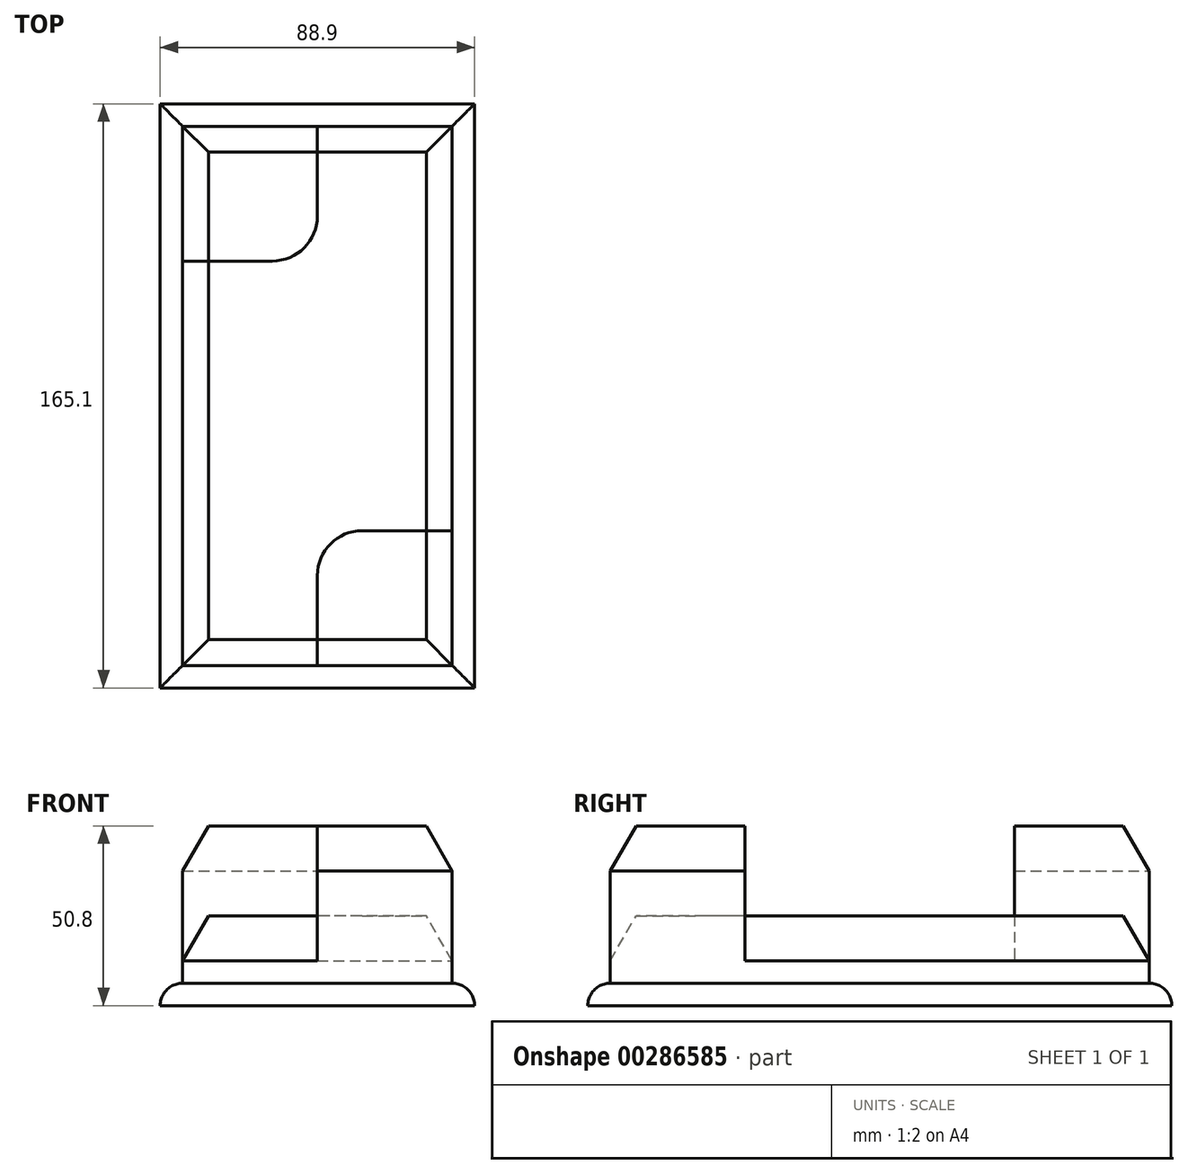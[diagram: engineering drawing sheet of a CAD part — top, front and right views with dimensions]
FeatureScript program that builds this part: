
annotation { "Feature Type Name" : "Feature", "Feature Type Description" : "" }
export const myFeature = defineFeature(function(context is Context, id is Id, definition is map)
    precondition{}
    {
        {
            var Q0;
            Q0=qCreatedBy(makeId("Top.planeOp"),FACE);
            var sketch = newSketch(context, id + "F0", { "sketchPlane" : qUnion([Q0])});
            skLineSegment(sketch, "E0.bottom", {"start": v(38.1, -76.2) * mm, "end": v(-38.1, -76.2) * mm});
            skLineSegment(sketch, "E0.top", {"start": v(38.1, 76.2) * mm, "end": v(-38.1, 76.2) * mm});
            skLineSegment(sketch, "E0.left", {"start": v(38.1, -76.2) * mm, "end": v(38.1, 76.2) * mm});
            skLineSegment(sketch, "E0.right", {"start": v(-38.1, -76.2) * mm, "end": v(-38.1, 76.2) * mm});
            skPoint(sketch, "E0.middle", {"position": v(0, 0) * mm});
            skLineSegment(sketch, "E1.0", {"start": v(44.45, -82.55) * mm, "end": v(44.45, 82.55) * mm});
            skLineSegment(sketch, "E2.0", {"start": v(44.45, 82.55) * mm, "end": v(-44.45, 82.55) * mm});
            skLineSegment(sketch, "E3.0", {"start": v(44.45, -82.55) * mm, "end": v(-44.45, -82.55) * mm});
            skLineSegment(sketch, "E4.0", {"start": v(-44.45, -82.55) * mm, "end": v(-44.45, 82.55) * mm});
            skLineSegment(sketch, "E5", {"start": v(38.1, -38.1) * mm, "end": v(12.7, -38.1) * mm});
            skLineSegment(sketch, "E6", {"start": v(0, -50.8) * mm, "end": v(0, -76.2) * mm});
            skLineSegment(sketch, "E7", {"start": v(0, 76.2) * mm, "end": v(0, 50.8) * mm});
            skLineSegment(sketch, "E8", {"start": v(-12.7, 38.1) * mm, "end": v(-38.1, 38.1) * mm});
            skPoint(sketch, "E9.visualSharp", {"position": v(0, 38.1) * mm});
            skArc(sketch, "E9.filletArc", {"start": v(-12.7, 38.1) * mm, "mid": v(-3.72, 41.82) * mm, "end": v(0, 50.8) * mm});
            skPoint(sketch, "E10.visualSharp", {"position": v(0, -38.1) * mm});
            skArc(sketch, "E10.filletArc", {"start": v(12.7, -38.1) * mm, "mid": v(3.72, -41.82) * mm, "end": v(0, -50.8) * mm});
            skSolve(sketch);
        }
        {
            var Q0;
            Q0 = qSketchRegion(id + "F0", true);
            var Q1;
            {var subQ3=sQuery(id+"F0.wireOp",EDGE,"E5");Q1=makeQuery(id+"F0.imprint","IMPRINT",FACE,{"disambiguationData":[TD([[makeQuery(id+"F0.imprint","IMPRINT",EDGE,{"derivedFrom":subQ3}),-1.0]])]});}
            var Q2;
            {var subQ1=sQuery(id+"F0.wireOp",EDGE,"E5");Q2=makeQuery(id+"F0.imprint","IMPRINT",FACE,{"disambiguationData":[TD([[makeQuery(id+"F0.imprint","IMPRINT",EDGE,{"derivedFrom":subQ1}),1.0]])]});}
            var Q3;
            {var subQ1=sQuery(id+"F0.wireOp",EDGE,"E7");Q3=makeQuery(id+"F0.imprint","IMPRINT",FACE,{"disambiguationData":[TD([[makeQuery(id+"F0.imprint","IMPRINT",EDGE,{"derivedFrom":subQ1}),-1.0]])]});}
            extrude(context, id + "F1", {"entities" : qUnion([Q0, Q1, Q2, Q3]), "depth" : 6.35 * mm});
        }
        {
            var Q0;
            {var subQ1=sQuery(id+"F0.wireOp",EDGE,"E7");Q0=makeQuery(id+"F0.imprint","IMPRINT",FACE,{"disambiguationData":[TD([[makeQuery(id+"F0.imprint","IMPRINT",EDGE,{"derivedFrom":subQ1}),-1.0]])]});}
            var Q1;
            {var subQ3=sQuery(id+"F0.wireOp",EDGE,"E5");Q1=makeQuery(id+"F0.imprint","IMPRINT",FACE,{"disambiguationData":[TD([[makeQuery(id+"F0.imprint","IMPRINT",EDGE,{"derivedFrom":subQ3}),-1.0]])]});}
            var Q2;
            {var subQ1=sQuery(id+"F0.wireOp",EDGE,"E5");Q2=makeQuery(id+"F0.imprint","IMPRINT",FACE,{"disambiguationData":[TD([[makeQuery(id+"F0.imprint","IMPRINT",EDGE,{"derivedFrom":subQ1}),1.0]])]});}
            extrude(context, id + "F2", {"entities" : qUnion([Q0, Q1, Q2]), "operationType" : NewBodyOperationType.ADD, "depth" : 25.4 * mm});
        }
        {
            var Q0;
            {var subQ1=sQuery(id+"F0.wireOp",EDGE,"E5");Q0=makeQuery(id+"F0.imprint","IMPRINT",FACE,{"disambiguationData":[TD([[makeQuery(id+"F0.imprint","IMPRINT",EDGE,{"derivedFrom":subQ1}),1.0]])]});}
            var Q1;
            {var subQ1=sQuery(id+"F0.wireOp",EDGE,"E7");Q1=makeQuery(id+"F0.imprint","IMPRINT",FACE,{"disambiguationData":[TD([[makeQuery(id+"F0.imprint","IMPRINT",EDGE,{"derivedFrom":subQ1}),-1.0]])]});}
            extrude(context, id + "F3", {"entities" : qUnion([Q0, Q1]), "operationType" : NewBodyOperationType.ADD, "depth" : 50.8 * mm});
        }
        {
            var Q0;
            Q0=makeQuery(id+"F1.opExtrude","CAP_EDGE",EDGE,{"disambiguationData":[OSD([sQuery(id+"F0.wireOp",EDGE,"E4.0")])],"isStart":false});
            var Q1;
            Q1=makeQuery(id+"F1.opExtrude","CAP_EDGE",EDGE,{"disambiguationData":[OSD([sQuery(id+"F0.wireOp",EDGE,"E3.0")])],"isStart":false});
            var Q2;
            Q2=makeQuery(id+"F1.opExtrude","CAP_EDGE",EDGE,{"disambiguationData":[OSD([sQuery(id+"F0.wireOp",EDGE,"E1.0")])],"isStart":false});
            var Q3;
            Q3=makeQuery(id+"F1.opExtrude","CAP_EDGE",EDGE,{"disambiguationData":[OSD([sQuery(id+"F0.wireOp",EDGE,"E2.0")])],"isStart":false});
            fillet(context, id + "F4", {"entities" : qUnion([Q0, Q1, Q2, Q3]), "radius" : 6.35 * mm, "tangentPropagation" : true, "allowEdgeOverflow" : false});
        }
        {
            var Q0;
            Q0=makeQuery(id+"F3.opExtrude","CAP_EDGE",EDGE,{"disambiguationData":[OSD([sQuery(id+"F0.wireOp",EDGE,"E0.right")])],"isStart":false});
            var Q1;
            Q1=makeQuery(id+"F3.opExtrude","CAP_EDGE",EDGE,{"disambiguationData":[OSD([sQuery(id+"F0.wireOp",EDGE,"E0.top")])],"isStart":false});
            chamfer(context, id + "F5", {"entities" : qUnion([Q0, Q1]), "chamferType" : ChamferType.OFFSET_ANGLE, "width" : 12.7 * mm, "oppositeDirection" : false, "angle" : 30 * degree, "tangentPropagation" : true});
        }
        {
            var Q0;
            Q0=makeQuery(id+"F3.opExtrude","CAP_EDGE",EDGE,{"disambiguationData":[OSD([sQuery(id+"F0.wireOp",EDGE,"E0.bottom")])],"isStart":false});
            var Q1;
            Q1=makeQuery(id+"F3.opExtrude","CAP_EDGE",EDGE,{"disambiguationData":[OSD([sQuery(id+"F0.wireOp",EDGE,"E0.left")])],"isStart":false});
            chamfer(context, id + "F6", {"entities" : qUnion([Q0, Q1]), "chamferType" : ChamferType.OFFSET_ANGLE, "width" : 12.7 * mm, "oppositeDirection" : false, "angle" : 30 * degree, "tangentPropagation" : true});
        }
        {
            var Q0;
            Q0=makeQuery(id+"F2.opExtrude","CAP_EDGE",EDGE,{"disambiguationData":[OSD([sQuery(id+"F0.wireOp",EDGE,"E0.bottom")])],"isStart":false});
            var Q1;
            Q1=makeQuery(id+"F2.opExtrude","CAP_EDGE",EDGE,{"disambiguationData":[OSD([sQuery(id+"F0.wireOp",EDGE,"E0.right")])],"isStart":false});
            chamfer(context, id + "F7", {"entities" : qUnion([Q0, Q1]), "chamferType" : ChamferType.OFFSET_ANGLE, "width" : 12.7 * mm, "oppositeDirection" : false, "angle" : 30 * degree, "tangentPropagation" : true});
        }
        {
            var Q0;
            Q0=makeQuery(id+"F2.opExtrude","CAP_EDGE",EDGE,{"disambiguationData":[OSD([sQuery(id+"F0.wireOp",EDGE,"E0.left")])],"isStart":false});
            var Q1;
            Q1=makeQuery(id+"F2.opExtrude","CAP_EDGE",EDGE,{"disambiguationData":[OSD([sQuery(id+"F0.wireOp",EDGE,"E0.top")])],"isStart":false});
            chamfer(context, id + "F8", {"entities" : qUnion([Q0, Q1]), "chamferType" : ChamferType.OFFSET_ANGLE, "width" : 12.7 * mm, "oppositeDirection" : true, "angle" : 30 * degree, "tangentPropagation" : true});
        }
    });
